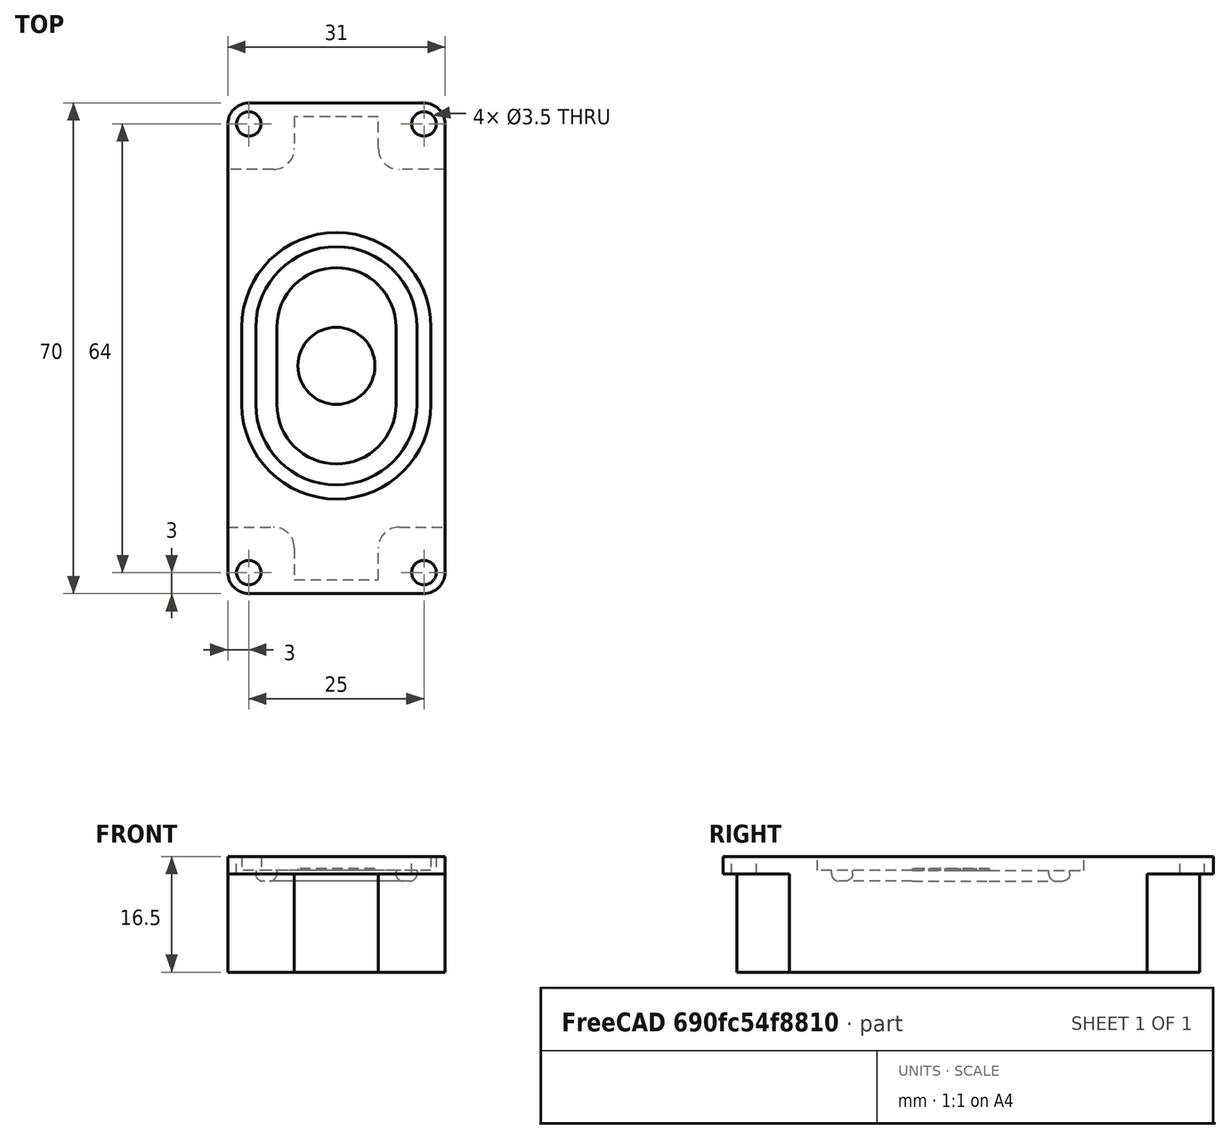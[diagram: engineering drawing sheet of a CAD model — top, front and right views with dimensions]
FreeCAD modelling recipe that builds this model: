
FCSTD DOCUMENT  (FreeCAD 0.21R33668 +26 (Git))
Label: Speaker_Part
License: All rights reserved
LicenseURL: https://en.wikipedia.org/wiki/All_rights_reserved
objects: TechDraw::DrawViewDimension×11, Sketcher::SketchObject×6, TechDraw::DrawProjGroupItem×4, PartDesign::Pad×3, PartDesign::Pocket×3, PartDesign::Fillet×3, PartDesign::Body×1, TechDraw::DrawSVGTemplate×1, TechDraw::DrawProjGroup×1, TechDraw::DrawPage×1
note: 45 computed .brp shape members not serialized (recipe doc carries the construction recipe); baked Part::Feature solids carry a one-line shape summary decoded from their .brp

FEATURE [Sketcher::SketchObject] Sketch
  FullyConstrained = true
  MapMode = 5
  Support = -> [XY_Plane]
  sketch-geometry (4):
    g0: LineSegment StartX=-15.5 StartY=70 StartZ=0 EndX=15.5 EndY=70 EndZ=0
    g1: LineSegment StartX=15.5 StartY=70 StartZ=0 EndX=15.5 EndY=0 EndZ=0
    g2: LineSegment StartX=15.5 StartY=0 StartZ=0 EndX=-15.5 EndY=0 EndZ=0
    g3: LineSegment StartX=-15.5 StartY=0 StartZ=0 EndX=-15.5 EndY=70 EndZ=0
  constraints (11):
    c: Coincident(g0,g1)
    c: Coincident(g1,g2)
    c: Coincident(g2,g3)
    c: Coincident(g3,g0)
    c: Horizontal(g2)
    c: Vertical(g1)
    c: Vertical(g3)
    c: PointOnObject(g1,g-1)
    c: DistanceY(g1,g1) = 70
    c: DistanceX(g0,g0) = 31
    c: Symmetric(g0,g0,g-2)
FEATURE [PartDesign::Pad] Pad
  Direction = (0,0,1)
  Length = 2.5
  Length2 = 10
  Profile = -> Sketch
  ReferenceAxis = -> Sketch [N_Axis]
  Type = 0
FEATURE [Sketcher::SketchObject] Sketch001
  ExternalGeometry = -> [Pad]
  FullyConstrained = true
  MapMode = 5
  Placement = pos=(0,0,2.5) rot=(0,0,1;0rad)
  Support = -> [Pad]
  sketch-geometry (6):
    g0: Circle CenterX=-12.5 CenterY=67 CenterZ=0 NormalX=0 NormalY=0 NormalZ=1 AngleXU=0 Radius=1.75
    g1: Circle CenterX=12.5 CenterY=67 CenterZ=0 NormalX=0 NormalY=0 NormalZ=1 AngleXU=0 Radius=1.75
    g2: Circle CenterX=-12.5 CenterY=3 CenterZ=0 NormalX=0 NormalY=0 NormalZ=1 AngleXU=0 Radius=1.75
    g3: Circle CenterX=12.5 CenterY=3 CenterZ=0 NormalX=0 NormalY=0 NormalZ=1 AngleXU=0 Radius=1.75
    g4: LineSegment StartX=-12.5 StartY=3 StartZ=0 EndX=12.5 EndY=3 EndZ=0
    g5: LineSegment StartX=-12.5 StartY=67 StartZ=0 EndX=12.5 EndY=67 EndZ=0
  constraints (14):
    c: Equal(g3,g2)
    c: Equal(g2,g0)
    c: Equal(g0,g1)
    c: Diameter(g0) = 3.5
    c: Symmetric(g0,g1,g-2)
    c: Symmetric(g2,g3,g-2)
    c: Coincident(g4,g2)
    c: Coincident(g4,g3)
    c: Coincident(g5,g0)
    c: Coincident(g5,g1)
    c: Equal(g4,g5)
    c: DistanceY(g-1,g3) = 3
    c: DistanceY(g1,g-3) = 3
    c: DistanceX(g1,g-3) = 3
FEATURE [PartDesign::Pocket] Pocket
  BaseFeature = -> Pad
  Direction = (0,0,-1)
  Length = 0
  Length2 = 5
  Profile = -> Sketch001
  ReferenceAxis = -> Sketch001 [N_Axis]
  Type = 3
  UpToFace = -> Pad [Face5]
FEATURE [PartDesign::Fillet] Fillet
  Base = -> Pocket [Edge5,Edge8,Edge1,Edge2]
  BaseFeature = -> Pocket
  Radius = 3
  SupportTransform = false
  UseAllEdges = false
FEATURE [Sketcher::SketchObject] Sketch002
  ExternalGeometry = -> [Fillet]
  FullyConstrained = true
  MapMode = 5
  Placement = pos=(0,0,0) rot=(1,0,0;3.14159rad)
  Support = -> [Fillet]
  sketch-geometry (12):
    g0: LineSegment StartX=-6 StartY=-2 StartZ=0 EndX=6 EndY=-2 EndZ=0
    g1: LineSegment StartX=6 StartY=-2 StartZ=0 EndX=6 EndY=-9.5 EndZ=0
    g2: LineSegment StartX=6 StartY=-9.5 StartZ=0 EndX=15.5 EndY=-9.5 EndZ=0
    g3: LineSegment StartX=15.5 StartY=-9.5 StartZ=0 EndX=15.5 EndY=-60.5 EndZ=0
    g4: LineSegment StartX=15.5 StartY=-60.5 StartZ=0 EndX=6 EndY=-60.5 EndZ=0
    g5: LineSegment StartX=6 StartY=-60.5 StartZ=0 EndX=6 EndY=-68 EndZ=0
    g6: LineSegment StartX=6 StartY=-68 StartZ=0 EndX=-6 EndY=-68 EndZ=0
    g7: LineSegment StartX=-6 StartY=-68 StartZ=0 EndX=-6 EndY=-60.5 EndZ=0
    g8: LineSegment StartX=-6 StartY=-60.5 StartZ=0 EndX=-15.5 EndY=-60.5 EndZ=0
    g9: LineSegment StartX=-15.5 StartY=-60.5 StartZ=0 EndX=-15.5 EndY=-9.5 EndZ=0
    g10: LineSegment StartX=-15.5 StartY=-9.5 StartZ=0 EndX=-6 EndY=-9.5 EndZ=0
    g11: LineSegment StartX=-6 StartY=-9.5 StartZ=0 EndX=-6 EndY=-2 EndZ=0
  constraints (32):
    c: Coincident(g1,g0)
    c: Vertical(g1)
    c: Coincident(g2,g1)
    c: Horizontal(g2)
    c: Coincident(g3,g2)
    c: Coincident(g4,g3)
    c: Horizontal(g4)
    c: Vertical(g5)
    c: Coincident(g6,g5)
    c: Coincident(g7,g6)
    c: Vertical(g7)
    c: Coincident(g9,g8)
    c: Vertical(g9)
    c: Coincident(g10,g9)
    c: Coincident(g11,g10)
    c: Coincident(g11,g0)
    c: Vertical(g11)
    c: Horizontal(g10)
    c: Horizontal(g8)
    c: Coincident(g8,g7)
    c: Coincident(g5,g4)
    c: Symmetric(g0,g0,g-2)
    c: Symmetric(g2,g9,g-2)
    c: Symmetric(g6,g5,g-2)
    c: Equal(g9,g3)
    c: Equal(g1,g5)
    c: DistanceY(g0,g-1) = 2
    c: Tangent(g3,g-4)
    c: DistanceY(g3,g3) = 51
    c: DistanceX(g0,g0) = 12
    c: Equal(g6,g0)
    c: DistanceY(g-3,g5) = 2
FEATURE [PartDesign::Pad] Pad001
  BaseFeature = -> Fillet
  Direction = (0,0,-1)
  Length = 14
  Length2 = 10
  Profile = -> Sketch002
  ReferenceAxis = -> Sketch002 [N_Axis]
  Type = 0
FEATURE [PartDesign::Fillet] Fillet001
  Base = -> Pad001 [Edge71,Edge72,Edge39,Edge33]
  BaseFeature = -> Pad001
  Radius = 3
  SupportTransform = false
  UseAllEdges = false
FEATURE [Sketcher::SketchObject] Sketch003
  FullyConstrained = true
  MapMode = 5
  Placement = pos=(0,0,2.5) rot=(0,0,1;0rad)
  Support = -> [Fillet001]
  sketch-geometry (4):
    g0: ArcOfCircle CenterX=0 CenterY=38 CenterZ=0 NormalX=0 NormalY=0 NormalZ=1 AngleXU=0 Radius=13.5 StartAngle=1e-16 EndAngle=3.14159
    g1: ArcOfCircle CenterX=0 CenterY=27 CenterZ=0 NormalX=0 NormalY=0 NormalZ=1 AngleXU=0 Radius=13.5 StartAngle=3.14159 EndAngle=6.28319
    g2: LineSegment StartX=-13.5 StartY=38 StartZ=0 EndX=-13.5 EndY=27 EndZ=0
    g3: LineSegment StartX=13.5 StartY=27 StartZ=0 EndX=13.5 EndY=38 EndZ=0
  constraints (10):
    c: Tangent(g0,g2) = -1.5708
    c: Tangent(g2,g1) = -1.5708
    c: Tangent(g1,g3) = -1.5708
    c: Tangent(g3,g0) = -1.5708
    c: Equal(g0,g1)
    c: PointOnObject(g0,g-2)
    c: PointOnObject(g1,g-2)
    c: DistanceX(g0,g0) = 27
    c: DistanceY(g1,g0) = 11
    c: DistanceY(g-1,g1) = 27
FEATURE [PartDesign::Pocket] Pocket001
  BaseFeature = -> Fillet001
  Direction = (0,0,-1)
  Length = 2
  Length2 = 5
  Profile = -> Sketch003
  ReferenceAxis = -> Sketch003 [N_Axis]
  Type = 0
FEATURE [Sketcher::SketchObject] Sketch004
  ExternalGeometry = -> [Pocket001]
  FullyConstrained = true
  MapMode = 5
  Placement = pos=(0,0,0.5) rot=(0,0,1;0rad)
  Support = -> [Pocket001]
  sketch-geometry (8):
    g0: ArcOfCircle CenterX=0 CenterY=38 CenterZ=0 NormalX=0 NormalY=0 NormalZ=1 AngleXU=0 Radius=11.5 StartAngle=2e-16 EndAngle=3.14159
    g1: ArcOfCircle CenterX=0 CenterY=27 CenterZ=0 NormalX=0 NormalY=0 NormalZ=1 AngleXU=0 Radius=11.5 StartAngle=3.14159 EndAngle=6.28319
    g2: LineSegment StartX=-11.5 StartY=38 StartZ=0 EndX=-11.5 EndY=27 EndZ=0
    g3: LineSegment StartX=11.5 StartY=27 StartZ=0 EndX=11.5 EndY=38 EndZ=0
    g4: ArcOfCircle CenterX=0 CenterY=38 CenterZ=0 NormalX=0 NormalY=0 NormalZ=1 AngleXU=0 Radius=8.5 StartAngle=2.1e-15 EndAngle=3.14159
    g5: ArcOfCircle CenterX=0 CenterY=27 CenterZ=0 NormalX=0 NormalY=0 NormalZ=1 AngleXU=0 Radius=8.5 StartAngle=3.14159 EndAngle=6.28319
    g6: LineSegment StartX=-8.5 StartY=38 StartZ=0 EndX=-8.5 EndY=27 EndZ=0
    g7: LineSegment StartX=8.5 StartY=27 StartZ=0 EndX=8.5 EndY=38 EndZ=0
  constraints (16):
    c: Tangent(g0,g2) = -1.5708
    c: Tangent(g2,g1) = -1.5708
    c: Tangent(g1,g3) = -1.5708
    c: Tangent(g3,g0) = -1.5708
    c: Equal(g0,g1)
    c: DistanceX(g0,g-3) = 2
    c: Coincident(g0,g-5)
    c: Coincident(g-4,g1)
    c: Tangent(g4,g6) = -1.5708
    c: Tangent(g6,g5) = -1.5708
    c: Tangent(g5,g7) = -1.5708
    c: Tangent(g7,g4) = -1.5708
    c: Equal(g4,g5)
    c: Coincident(g5,g1)
    c: Coincident(g4,g0)
    c: DistanceX(g4,g0) = 3
FEATURE [PartDesign::Pocket] Pocket002
  BaseFeature = -> Pocket001
  Direction = (0,0,-1)
  Length = 1.5
  Length2 = 5
  Profile = -> Sketch004
  ReferenceAxis = -> Sketch004 [N_Axis]
  Type = 0
FEATURE [PartDesign::Fillet] Fillet002
  Base = -> Pocket002 [Edge105,Edge109,Edge107,Edge111,Edge114,Edge113,Edge112,Edge110]
  BaseFeature = -> Pocket002
  Radius = 1
  SupportTransform = false
  UseAllEdges = false
FEATURE [Sketcher::SketchObject] Sketch005
  ExternalGeometry = -> [Fillet002]
  FullyConstrained = true
  MapMode = 5
  Placement = pos=(0,0,0.5) rot=(0,0,1;0rad)
  Support = -> [Fillet002]
  sketch-geometry (3):
    g0: Circle CenterX=0 CenterY=32.5 CenterZ=0 NormalX=0 NormalY=0 NormalZ=1 AngleXU=0 Radius=5.5
    g1: LineSegment StartX=0 StartY=38 StartZ=0 EndX=0 EndY=32.5 EndZ=0
    g2: LineSegment StartX=0 StartY=32.5 StartZ=0 EndX=0 EndY=27 EndZ=0
  constraints (7):
    c: PointOnObject(g0,g-2)
    c: Coincident(g1,g-3)
    c: Coincident(g1,g0)
    c: Coincident(g2,g0)
    c: Coincident(g2,g-4)
    c: PointOnObject(g1,g0)
    c: PointOnObject(g2,g0)
FEATURE [PartDesign::Pad] Pad002
  BaseFeature = -> Fillet002
  Direction = (0,0,1)
  Length = 0.3
  Length2 = 10
  Profile = -> Sketch005
  ReferenceAxis = -> Sketch005 [N_Axis]
  Type = 0
FEATURE [PartDesign::Body] Body
  Group = -> [Sketch,Pad,Sketch001,Pocket,Fillet,Sketch002,Pad001,Fillet001,Sketch003,Pocket001,Sketch004,Pocket002,Fillet002,Sketch005,Pad002]
  Origin = -> Origin
  Tip = -> Pad002
FEATURE [TechDraw::DrawSVGTemplate] Template
  EditableTexts = Designed_by_Name=Alex Hold; Drawing_number=Drawing number; FC-Date=23.09.14; FC-SC=Scale; FC-SH=Sheet; FC-Title=Speaker Part; Subtitle=Subtitle; Weight=Weight
  Height = 210
  Orientation = 1
  Template = C:/Program Files/FreeCAD 0.21/data/Mod/TechDraw/Templates/A4_LandscapeTD.svg
  Width = 297
FEATURE [TechDraw::DrawProjGroupItem] ProjItem  label="Front"
  CoarseView = false
  Direction = (0,0,1)
  Focus = 100
  HardHidden = false
  IsoCount = 0
  IsoHidden = false
  IsoVisible = false
  LockPosition = true
  Perspective = false
  Rotation = 0
  RotationVector = (-1,0,0)
  ScaleType = 2
  ScrubCount = 0
  SeamHidden = false
  SeamVisible = false
  SmoothHidden = false
  SmoothVisible = true
  Source = -> [Body]
  Type = 0
  X = 0
  XDirection = (-1,0,0)
  Y = 0
FEATURE [TechDraw::DrawProjGroupItem] ProjItem001  label="Rear"
  CoarseView = false
  Direction = (0,0,-1)
  Focus = 100
  HardHidden = false
  IsoCount = 0
  IsoHidden = false
  IsoVisible = false
  LockPosition = false
  Perspective = false
  Rotation = 0
  RotationVector = (1,0,0)
  ScaleType = 2
  ScrubCount = 0
  SeamHidden = false
  SeamVisible = false
  SmoothHidden = false
  SmoothVisible = true
  Source = -> [Body]
  Type = 3
  X = 94.5876
  XDirection = (1,0,0)
  Y = 0
FEATURE [TechDraw::DrawViewDimension] Dimension
  AngleOverride = false
  Arbitrary = false
  ArbitraryTolerances = false
  EqualTolerance = true
  ExtensionAngle = 0
  FormatSpec = %.2w
  FormatSpecOverTolerance = %+.2w
  FormatSpecUnderTolerance = %+.2w
  Inverted = false
  LineAngle = 0
  LockPosition = false
  MeasureType = 1
  OverTolerance = 0
  References2D = -> [ProjItem]
  Rotation = 0
  ScaleType = 0
  TheoreticalExact = false
  Type = 2
  UnderTolerance = 0
  X = 29.1366
  Y = 2.5
FEATURE [TechDraw::DrawViewDimension] Dimension001
  AngleOverride = false
  Arbitrary = false
  ArbitraryTolerances = false
  EqualTolerance = true
  ExtensionAngle = 0
  FormatSpec = %.2w
  FormatSpecOverTolerance = %+.2w
  FormatSpecUnderTolerance = %+.2w
  Inverted = false
  LineAngle = 0
  LockPosition = false
  MeasureType = 1
  OverTolerance = 0
  References2D = -> [ProjItem]
  Rotation = 0
  ScaleType = 0
  TheoreticalExact = false
  Type = 1
  UnderTolerance = 0
  X = -0.470848
  Y = 54.5895
FEATURE [TechDraw::DrawProjGroupItem] ProjItem002  label="FrontBottomLeft"
  CoarseView = false
  Direction = (0.57735,0.57735,0.57735)
  Focus = 100
  HardHidden = false
  IsoCount = 0
  IsoHidden = false
  IsoVisible = false
  LockPosition = false
  Perspective = false
  Rotation = 0
  RotationVector = (1,0,0)
  ScaleType = 2
  ScrubCount = 0
  SeamHidden = false
  SeamVisible = false
  SmoothHidden = false
  SmoothVisible = true
  Source = -> [Body]
  Type = 8
  X = 47.2938
  XDirection = (-0.707107,0,0.707107)
  Y = 85.0498
FEATURE [TechDraw::DrawProjGroupItem] ProjItem003  label="Left"
  CoarseView = false
  Direction = (1,0,1e-16)
  Focus = 100
  HardHidden = false
  IsoCount = 0
  IsoHidden = false
  IsoVisible = false
  LockPosition = false
  Perspective = false
  Rotation = 0
  RotationVector = (1,0,0)
  ScaleType = 2
  ScrubCount = 0
  SeamHidden = false
  SeamVisible = false
  SmoothHidden = false
  SmoothVisible = true
  Source = -> [Body]
  Type = 1
  X = 47.2938
  XDirection = (-1e-16,0,1)
  Y = 0
FEATURE [TechDraw::DrawProjGroup] ProjGroup
  Anchor = -> ProjItem
  AutoDistribute = true
  LockPosition = false
  ProjectionType = 0
  Rotation = 0
  ScaleType = 0
  Source = -> [Body]
  Views = -> [ProjItem,ProjItem001,ProjItem002,ProjItem003]
  X = 43.8997
  Y = 143.231
  spacingX = 15
  spacingY = 15
FEATURE [TechDraw::DrawViewDimension] Dimension002
  AngleOverride = false
  Arbitrary = false
  ArbitraryTolerances = false
  EqualTolerance = true
  ExtensionAngle = 0
  FormatSpec = %.2w
  FormatSpecOverTolerance = %+.2w
  FormatSpecUnderTolerance = %+.2w
  Inverted = false
  LineAngle = 0
  LockPosition = false
  MeasureType = 1
  OverTolerance = 0
  References2D = -> [ProjItem003]
  Rotation = 0
  ScaleType = 0
  TheoreticalExact = false
  Type = 1
  UnderTolerance = 0
  X = 19.0078
  Y = -43.089
FEATURE [TechDraw::DrawViewDimension] Dimension003
  AngleOverride = false
  Arbitrary = false
  ArbitraryTolerances = false
  EqualTolerance = true
  ExtensionAngle = 0
  FormatSpec = %.2w
  FormatSpecOverTolerance = %+.2w
  FormatSpecUnderTolerance = %+.2w
  Inverted = false
  LineAngle = 0
  LockPosition = false
  MeasureType = 1
  OverTolerance = 0
  References2D = -> [ProjItem003]
  Rotation = 0
  ScaleType = 0
  TheoreticalExact = false
  Type = 1
  UnderTolerance = 0
  X = -16.4692
  Y = 50.2005
FEATURE [TechDraw::DrawViewDimension] Dimension004
  AngleOverride = false
  Arbitrary = false
  ArbitraryTolerances = false
  EqualTolerance = true
  ExtensionAngle = 0
  FormatSpec = %.2w
  FormatSpecOverTolerance = %+.2w
  FormatSpecUnderTolerance = %+.2w
  Inverted = false
  LineAngle = 0
  LockPosition = false
  MeasureType = 1
  OverTolerance = 0
  References2D = -> [ProjItem001]
  Rotation = 0
  ScaleType = 0
  TheoreticalExact = false
  Type = 2
  UnderTolerance = 0
  X = 29.9757
  Y = 42.4996
FEATURE [TechDraw::DrawViewDimension] Dimension005
  AngleOverride = false
  Arbitrary = false
  ArbitraryTolerances = false
  EqualTolerance = true
  ExtensionAngle = 0
  FormatSpec = %.2w
  FormatSpecOverTolerance = %+.2w
  FormatSpecUnderTolerance = %+.2w
  Inverted = false
  LineAngle = 0
  LockPosition = false
  MeasureType = 1
  OverTolerance = 0
  References2D = -> [ProjItem001]
  Rotation = 0
  ScaleType = 0
  TheoreticalExact = false
  Type = 2
  UnderTolerance = 0
  X = 24.5216
  Y = -38.045
FEATURE [TechDraw::DrawViewDimension] Dimension006
  AngleOverride = false
  Arbitrary = false
  ArbitraryTolerances = false
  EqualTolerance = true
  ExtensionAngle = 0
  FormatSpec = %.2w
  FormatSpecOverTolerance = %+.2w
  FormatSpecUnderTolerance = %+.2w
  Inverted = false
  LineAngle = 0
  LockPosition = false
  MeasureType = 1
  OverTolerance = 0
  References2D = -> [ProjItem001]
  Rotation = 0
  ScaleType = 0
  TheoreticalExact = false
  Type = 2
  UnderTolerance = 0
  X = 22.4086
  Y = 3.22722
FEATURE [TechDraw::DrawViewDimension] Dimension007
  AngleOverride = false
  Arbitrary = false
  ArbitraryTolerances = false
  EqualTolerance = true
  ExtensionAngle = 0
  FormatSpec = ⌀%.2w
  FormatSpecOverTolerance = %+.2w
  FormatSpecUnderTolerance = %+.2w
  Inverted = false
  LineAngle = 0
  LockPosition = false
  MeasureType = 1
  OverTolerance = 0
  References2D = -> [ProjItem]
  Rotation = 0
  ScaleType = 0
  TheoreticalExact = false
  Type = 5
  UnderTolerance = 0
  X = 25.5079
  Y = 51.3726
FEATURE [TechDraw::DrawViewDimension] Dimension008
  AngleOverride = false
  Arbitrary = false
  ArbitraryTolerances = false
  EqualTolerance = true
  ExtensionAngle = 0
  FormatSpec = %.2w
  FormatSpecOverTolerance = %+.2w
  FormatSpecUnderTolerance = %+.2w
  Inverted = false
  LineAngle = 0
  LockPosition = false
  MeasureType = 1
  OverTolerance = 0
  References2D = -> [ProjItem001]
  Rotation = 0
  ScaleType = 0
  TheoreticalExact = false
  Type = 1
  UnderTolerance = 0
  X = -0.683648
  Y = 49.6287
FEATURE [TechDraw::DrawViewDimension] Dimension009
  AngleOverride = false
  Arbitrary = false
  ArbitraryTolerances = false
  EqualTolerance = true
  ExtensionAngle = 0
  FormatSpec = %.2w
  FormatSpecOverTolerance = %+.2w
  FormatSpecUnderTolerance = %+.2w
  Inverted = false
  LineAngle = 0
  LockPosition = false
  MeasureType = 1
  OverTolerance = 0
  References2D = -> [ProjItem]
  Rotation = 0
  ScaleType = 0
  TheoreticalExact = false
  Type = 1
  UnderTolerance = 0
  X = 26.1103
  Y = -39.7937
FEATURE [TechDraw::DrawViewDimension] Dimension010
  AngleOverride = false
  Arbitrary = false
  ArbitraryTolerances = false
  EqualTolerance = true
  ExtensionAngle = 0
  FormatSpec = %.2w
  FormatSpecOverTolerance = %+.2w
  FormatSpecUnderTolerance = %+.2w
  Inverted = false
  LineAngle = 0
  LockPosition = false
  MeasureType = 1
  OverTolerance = 0
  References2D = -> [ProjItem]
  Rotation = 0
  ScaleType = 0
  TheoreticalExact = false
  Type = 2
  UnderTolerance = 0
  X = 22.9451
  Y = -25.3233
FEATURE [TechDraw::DrawPage] Page
  KeepUpdated = true
  NextBalloonIndex = 2
  ProjectionType = 0
  Template = -> Template
  Views = -> [ProjGroup,Dimension,Dimension001,Dimension002,Dimension003,Dimension004,Dimension005,Dimension006,Dimension007,Dimension008,Dimension009,Dimension010]
